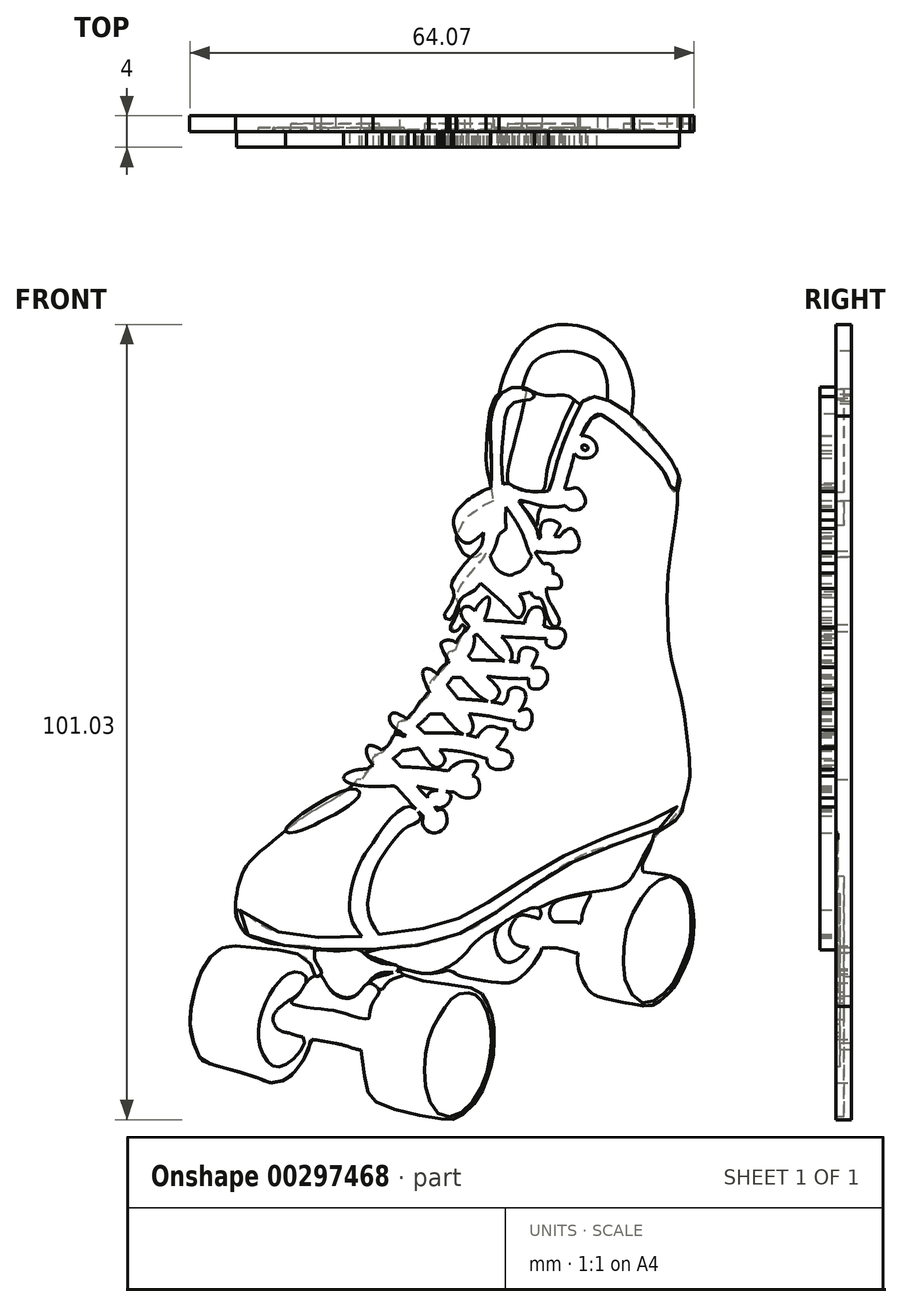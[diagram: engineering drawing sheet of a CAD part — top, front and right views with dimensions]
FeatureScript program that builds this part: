
annotation { "Feature Type Name" : "Feature", "Feature Type Description" : "" }
export const myFeature = defineFeature(function(context is Context, id is Id, definition is map)
    precondition{}
    {
        {
            var Q0;
            Q0=qCreatedBy(makeId("Front.planeOp"),FACE);
            var sketch = newSketch(context, id + "F0", { "sketchPlane" : qUnion([Q0])});
            skFitSpline(sketch, "E0", {"points": [v(-12.66, 16.22) * mm, v(-11.45, 15.9) * mm, v(-10.21, 15.64) * mm, v(-8.9, 15.37) * mm, v(-7.7, 15.13) * mm, v(-6.64, 14.98) * mm, v(-5.56, 15.1) * mm, v(-4.67, 15.72) * mm, v(-3.66, 16.57) * mm, v(-2.88, 17.5) * mm, v(-2.22, 18.59) * mm, v(-1.68, 19.8) * mm, v(-1.06, 21.19) * mm, v(-0.67, 22.58) * mm, v(-0.6, 23.51) * mm, v(-0.4, 25.03) * mm, v(-0.44, 26.3) * mm, v(-0.6, 27.55) * mm, v(-0.83, 28.64) * mm, v(-1.33, 30) * mm, v(-2.07, 30.88) * mm, v(-3.3, 31.47) * mm, v(-4.9, 31.78) * mm, v(-6.06, 31.97) * mm, v(-7.19, 32.17) * mm, v(-7.07, 32.9) * mm, v(-6.22, 34.57) * mm, v(-5.64, 36.04) * mm, v(-5.44, 36.86) * mm, v(-4.55, 37.44) * mm, v(-3.3, 38.18) * mm, v(-2.5, 38.8) * mm, v(-1.91, 39.61) * mm, v(-1.83, 40.62) * mm, v(-1.49, 41.24) * mm, v(-1.17, 42.64) * mm, v(-0.9, 44.35) * mm, v(-1.1, 47.49) * mm, v(-1.56, 51.33) * mm, v(-2.1, 54.51) * mm, v(-2.84, 57.19) * mm, v(-3.58, 60.72) * mm, v(-3.7, 63.04) * mm, v(-3.81, 67.66) * mm, v(-3.5, 71.7) * mm, v(-3.11, 74.18) * mm, v(-2.73, 76.66) * mm, v(-2.53, 79.03) * mm, v(-2.53, 80.07) * mm, v(-2.18, 81.24) * mm, v(-2.38, 82.79) * mm, v(-3.11, 83.92) * mm, v(-4.33, 85.57) * mm, v(-4.87, 86.43) * mm, v(-6.4, 87.78) * mm, v(-8.4, 89.91) * mm, v(-11.37, 91.78) * mm, v(-13.45, 92.22) * mm, v(-14.5, 91.87) * mm, v(-14.91, 91.44) * mm], "startDerivative": vector(80.46, -21.54) * mm, "endDerivative": vector(-30.96, -32.86) * mm});
            skFitSpline(sketch, "E1", {"points": [v(-14.91, 91.44) * mm, v(-16.65, 92.56) * mm, v(-18.46, 92.53) * mm, v(-20.26, 92.8) * mm, v(-21.34, 93.2) * mm, v(-23.4, 93.4) * mm, v(-25.2, 92.68) * mm, v(-25.7, 92.13) * mm, v(-26.31, 90.55) * mm, v(-26.58, 88.8) * mm, v(-26.74, 86.55) * mm, v(-26.78, 83.87) * mm, v(-26.5, 82.32) * mm, v(-26.2, 80.85) * mm, v(-25.92, 79.14) * mm], "startDerivative": vector(-22.92, 17.02) * mm, "endDerivative": vector(3.64, -24.68) * mm});
            skFitSpline(sketch, "E2", {"points": [v(-25.92, 79.14) * mm, v(-27.05, 78.6) * mm, v(-28.37, 77.7) * mm, v(-29.57, 76.73) * mm, v(-30.27, 75.41) * mm, v(-30.58, 74.37) * mm, v(-30.15, 73.32) * mm, v(-29.53, 72.39) * mm, v(-27.9, 71.77) * mm], "startDerivative": vector(-9.85, -4.24) * mm, "endDerivative": vector(11.11, -2.3) * mm});
            skFitSpline(sketch, "E3", {"points": [v(-28.83, 72.02) * mm, v(-28.34, 72.02) * mm, v(-27.85, 72.2) * mm, v(-27.2, 72.69) * mm, v(-27.05, 72.8) * mm, v(-26.89, 72.63) * mm, v(-26.92, 72.4) * mm, v(-27.27, 71.8) * mm, v(-27.89, 71.1) * mm, v(-28.43, 70.49) * mm, v(-29.17, 69.6) * mm, v(-29.71, 68.93) * mm, v(-30.15, 68.25) * mm, v(-30.5, 67.42) * mm, v(-30.62, 66.83) * mm, v(-30.36, 66.18) * mm, v(-30.31, 65.58) * mm, v(-30.53, 64.8) * mm, v(-30.93, 63.95) * mm, v(-31.36, 63.13) * mm, v(-31.2, 62.64) * mm, v(-30.68, 62.59) * mm, v(-30.37, 62.78) * mm, v(-30.08, 63.16) * mm, v(-29.81, 63.44) * mm, v(-29.54, 63.27) * mm, v(-29.5, 62.97) * mm, v(-29.62, 62.65) * mm, v(-29.94, 62.04) * mm, v(-30.25, 61.4) * mm, v(-30.47, 60.84) * mm, v(-30.65, 60.3) * mm, v(-31.49, 59.99) * mm, v(-31.86, 59.32) * mm, v(-31.84, 58.65) * mm, v(-32.17, 57.9) * mm, v(-33.63, 56.5) * mm, v(-34.14, 55.35) * mm, v(-34.1, 54.69) * mm, v(-35.05, 53.56) * mm, v(-35.98, 52.36) * mm, v(-37.1, 51.22) * mm, v(-37.91, 51.08) * mm, v(-38.38, 49.63) * mm, v(-40.18, 47.13) * mm, v(-41.12, 46.75) * mm, v(-41.24, 45.74) * mm, v(-42.4, 44.21) * mm, v(-42.56, 43.8) * mm, v(-43.08, 43.77) * mm, v(-44.07, 42.74) * mm, v(-49.8, 39.14) * mm, v(-54.36, 35.56) * mm, v(-57.32, 32.68) * mm, v(-58.52, 29) * mm, v(-58.33, 25.74) * mm, v(-55.92, 23.57) * mm, v(-52.02, 22.75) * mm, v(-48.7, 22.33) * mm, v(-48.59, 20.97) * mm, v(-47.75, 19.14) * mm, v(-48.48, 18.81) * mm, v(-49, 20.13) * mm, v(-50.97, 21.7) * mm, v(-55.18, 22.29) * mm, v(-59.17, 22.65) * mm, v(-60.7, 22.18) * mm, v(-62.47, 20.38) * mm, v(-63.78, 17.12) * mm, v(-64.4, 13.87) * mm, v(-64.22, 11.12) * mm, v(-63.24, 8.52) * mm, v(-62.47, 7.86) * mm, v(-55.44, 5.77) * mm, v(-55, 5.48) * mm, v(-53.6, 5.23) * mm, v(-51.7, 6.07) * mm, v(-50.42, 7.57) * mm, v(-49.43, 9.33) * mm, v(-49.07, 10.68) * mm, v(-48.74, 10.76) * mm, v(-42.84, 9.51) * mm, v(-42.62, 9.1) * mm, v(-42, 4.75) * mm, v(-40.31, 2.56) * mm, v(-32.22, 0.62) * mm, v(-30.5, 0.8) * mm, v(-28.01, 2.96) * mm, v(-26.58, 6.1) * mm, v(-26, 8.2) * mm, v(-25.78, 10.94) * mm, v(-26, 13.65) * mm, v(-26.99, 16) * mm, v(-28.49, 17.24) * mm, v(-36.87, 18.74) * mm, v(-37.71, 19.66) * mm, v(-34.13, 19.07) * mm, v(-31.53, 19.5) * mm, v(-30.43, 18.96) * mm, v(-25.56, 18) * mm, v(-22.63, 18.49) * mm, v(-19.8, 22.07) * mm, v(-19.63, 22.44) * mm, v(-15.27, 21.9) * mm, v(-15.2, 21.2) * mm, v(-14.9, 19.15) * mm, v(-13.66, 16.91) * mm, v(-12.66, 16.22) * mm], "startDerivative": vector(99.24, -6.04) * mm, "endDerivative": vector(125.3, -64.7) * mm});
            skFitSpline(sketch, "E4", {"points": [v(-25.2, 92.68) * mm, v(-20.46, 100.62) * mm, v(-11.73, 100) * mm, v(-8.4, 89.91) * mm], "startDerivative": vector(5.78, 27.5) * mm, "endDerivative": vector(-8.42, -35.04) * mm});
            skFitSpline(sketch, "E5", {"points": [v(-22.25, 93.4) * mm, v(-19.97, 97.43) * mm, v(-12.94, 97.22) * mm, v(-11.37, 91.78) * mm], "startDerivative": vector(4.24, 16.05) * mm, "endDerivative": vector(-0.4, -21.14) * mm});
            skSolve(sketch);
        }
        {
            var Q0;
            Q0=qCreatedBy(makeId("Front.planeOp"),FACE);
            var sketch = newSketch(context, id + "F1", { "sketchPlane" : qUnion([Q0])});
            skFitSpline(sketch, "E6", {"points": [v(-20.8, 94.94) * mm, v(-21.53, 93.88) * mm, v(-22.17, 90.77) * mm, v(-23.27, 86.35) * mm, v(-24.08, 81.7) * mm, v(-23.14, 80.94) * mm, v(-19.78, 80.34) * mm, v(-19.1, 82.9) * mm, v(-18, 86.43) * mm, v(-16.59, 90.05) * mm, v(-15.19, 93.62) * mm, v(-17.02, 94.56) * mm, v(-20.8, 94.94) * mm]});
            skFitSpline(sketch, "E7", {"points": [v(-22.28, 78.98) * mm, v(-19.9, 78.56) * mm, v(-20.09, 77.84) * mm, v(-20.39, 76.06) * mm, v(-21.32, 77.45) * mm, v(-22.28, 78.98) * mm]});
            skSolve(sketch);
        }
        {
            var Q0;
            Q0=qCreatedBy(makeId("Front.planeOp"),FACE);
            var sketch = newSketch(context, id + "F2", { "sketchPlane" : qUnion([Q0])});
            skFitSpline(sketch, "E8", {"points": [v(-22.6, 80.66) * mm, v(-19.23, 80.38) * mm, v(-16.76, 80.7) * mm, v(-15.8, 80.41) * mm, v(-15.58, 79.34) * mm, v(-16.8, 78.59) * mm, v(-19.44, 78.48) * mm, v(-22.6, 79.16) * mm, v(-22.09, 78.34) * mm, v(-21.12, 76.83) * mm, v(-20.37, 75.51) * mm, v(-20.2, 73.97) * mm, v(-20.55, 72.54) * mm, v(-21.02, 72.11) * mm, v(-21.55, 71.1) * mm, v(-22.27, 70.32) * mm, v(-23.27, 69.9) * mm, v(-23.92, 69.71) * mm, v(-25.45, 70.54) * mm, v(-26.31, 72.15) * mm, v(-27, 74.22) * mm, v(-27.14, 75.87) * mm, v(-26.67, 77.84) * mm, v(-25.96, 79.27) * mm, v(-24.52, 80.34) * mm, v(-23.63, 79.7) * mm, v(-23.13, 80.8) * mm, v(-22.6, 80.66) * mm]});
            skFitSpline(sketch, "E9", {"points": [v(-23.63, 79.7) * mm, v(-22.6, 79.16) * mm], "startDerivative": vector(1.04, -0.54) * mm, "endDerivative": vector(1.04, -0.54) * mm});
            skFitSpline(sketch, "E10", {"points": [v(-23.63, 79.7) * mm, v(-25.35, 76.3) * mm, v(-25.96, 74.9) * mm, v(-26.31, 72.15) * mm], "startDerivative": vector(-4.78, -9.57) * mm, "endDerivative": vector(-0.75, -8.95) * mm});
            skFitSpline(sketch, "E11", {"points": [v(-24.27, 78.41) * mm, v(-22.23, 75.12) * mm, v(-21.52, 73.04) * mm, v(-21.02, 72.11) * mm], "startDerivative": vector(5.39, -7.68) * mm, "endDerivative": vector(2.3, -3.63) * mm});
            skFitSpline(sketch, "E12", {"points": [v(-23.13, 80.8) * mm, v(-23.99, 81.38) * mm, v(-24.85, 81.17) * mm, v(-25.24, 80.8) * mm, v(-25.01, 80.25) * mm], "startDerivative": vector(-2.81, 2.66) * mm, "endDerivative": vector(1.71, -2.68) * mm});
            skFitSpline(sketch, "E13", {"points": [v(-25.24, 80.8) * mm, v(-26.31, 80.8) * mm, v(-30.07, 78.41) * mm, v(-30.9, 75.94) * mm, v(-29.43, 73.83) * mm, v(-27.15, 75.12) * mm], "startDerivative": vector(-6.78, 1.52) * mm, "endDerivative": vector(11.72, 10.78) * mm});
            skFitSpline(sketch, "E14", {"points": [v(-25.24, 80.8) * mm, v(-27.46, 79.16) * mm, v(-29.32, 76.94) * mm, v(-30.9, 75.94) * mm], "startDerivative": vector(-6.64, -4.1) * mm, "endDerivative": vector(-5.59, -2.73) * mm});
            skFitSpline(sketch, "E15", {"points": [v(-24.27, 78.41) * mm, v(-24.27, 75.62) * mm, v(-23.13, 72.11) * mm, v(-21.52, 73.04) * mm], "startDerivative": vector(-0.53, -7.18) * mm, "endDerivative": vector(6.33, 6.23) * mm});
            skFitSpline(sketch, "E16", {"points": [v(-24.27, 75.62) * mm, v(-25.14, 74.83) * mm, v(-25.63, 73.4) * mm, v(-26.31, 72.15) * mm], "startDerivative": vector(-3.21, -2.14) * mm, "endDerivative": vector(-2.25, -3.47) * mm});
            skFitSpline(sketch, "E17", {"points": [v(-25.63, 73.4) * mm, v(-23.87, 73.4) * mm], "startDerivative": vector(1.77, 0) * mm, "endDerivative": vector(1.77, 0) * mm});
            skFitSpline(sketch, "E18", {"points": [v(-27.15, 75.12) * mm, v(-27.46, 73.4) * mm, v(-29.25, 71.5) * mm, v(-30.9, 69.25) * mm, v(-31.22, 68.39) * mm, v(-30.9, 67.35) * mm, v(-31.54, 65.6) * mm, v(-32.15, 64.49) * mm, v(-31.4, 64.1) * mm, v(-30.29, 66.2) * mm, v(-29.6, 67.06) * mm, v(-27.94, 68.1) * mm, v(-26.31, 72.15) * mm], "startDerivative": vector(-0.42, -21.79) * mm, "endDerivative": vector(9.61, 37.07) * mm});
            skFitSpline(sketch, "E19", {"points": [v(-20.18, 74.4) * mm, v(-16.72, 74.4) * mm, v(-16.18, 73.4) * mm, v(-17.58, 72.61) * mm, v(-20.44, 72.74) * mm], "startDerivative": vector(12.88, 1.9) * mm, "endDerivative": vector(-10.29, 1.45) * mm});
            skFitSpline(sketch, "E20", {"points": [v(-20.55, 72.54) * mm, v(-19.66, 71.32) * mm, v(-18.94, 70.32) * mm, v(-19.15, 68.1) * mm, v(-18.69, 66.24) * mm, v(-17.5, 63.63) * mm, v(-18.37, 63.27) * mm, v(-19.87, 66.74) * mm, v(-20.55, 66.88) * mm, v(-22.27, 70) * mm], "startDerivative": vector(8.72, -13.24) * mm, "endDerivative": vector(-11.7, 29.04) * mm});
            skFitSpline(sketch, "E21", {"points": [v(-22.27, 70) * mm, v(-22.27, 70.32) * mm], "startDerivative": vector(0, 0.32) * mm, "endDerivative": vector(0, 0.32) * mm});
            skFitSpline(sketch, "E22", {"points": [v(-18.9, 70) * mm, v(-17.58, 69.64) * mm, v(-17.33, 68.28) * mm, v(-19.15, 68.1) * mm], "startDerivative": vector(4.73, -0.06) * mm, "endDerivative": vector(-6.4, 0.81) * mm});
            skFitSpline(sketch, "E23", {"points": [v(-27.5, 68.68) * mm, v(-23.99, 65.45) * mm, v(-22.6, 64.34) * mm, v(-21.98, 66.06) * mm, v(-26.73, 70.54) * mm], "startDerivative": vector(13.18, -11.25) * mm, "endDerivative": vector(-19.34, 12.92) * mm});
            skFitSpline(sketch, "E24", {"points": [v(-24.51, 69.06) * mm, v(-22.02, 69.4) * mm], "startDerivative": vector(2.5, 0.34) * mm, "endDerivative": vector(2.5, 0.34) * mm});
            skFitSpline(sketch, "E25", {"points": [v(-22.6, 67.26) * mm, v(-21.19, 67.59) * mm], "startDerivative": vector(1.4, 0.33) * mm, "endDerivative": vector(1.4, 0.33) * mm});
            skFitSpline(sketch, "E26", {"points": [v(-27, 68.1) * mm, v(-27.15, 66.38) * mm, v(-25.01, 66.49) * mm], "startDerivative": vector(-1.36, -4.53) * mm, "endDerivative": vector(5.2, 1.2) * mm});
            skFitSpline(sketch, "E27", {"points": [v(-30.04, 65.06) * mm, v(-29.28, 65.78) * mm, v(-28.35, 65.3) * mm, v(-27.15, 64.02) * mm, v(-23.63, 60.2) * mm, v(-23.99, 58.72) * mm, v(-27.53, 61.77) * mm, v(-30.04, 65.06) * mm]});
            skFitSpline(sketch, "E28", {"points": [v(-27.15, 64.02) * mm, v(-20.2, 63.41) * mm, v(-18.37, 62.7) * mm, v(-18, 61.84) * mm, v(-19.15, 61.66) * mm, v(-24.86, 61.93) * mm], "startDerivative": vector(25.61, -1.63) * mm, "endDerivative": vector(-23.17, 1.13) * mm});
            skFitSpline(sketch, "E29", {"points": [v(-28.97, 63.27) * mm, v(-29.5, 61.95) * mm, v(-27.94, 62.2) * mm], "startDerivative": vector(-2.08, -3.5) * mm, "endDerivative": vector(4.1, 1.3) * mm});
            skFitSpline(sketch, "E30", {"points": [v(-32.54, 60.76) * mm, v(-32.15, 61.37) * mm, v(-30.9, 61.3) * mm, v(-27.53, 57.69) * mm, v(-25.14, 55) * mm, v(-25.63, 53.93) * mm, v(-27, 53.9) * mm, v(-32.54, 60.76) * mm]});
            skFitSpline(sketch, "E31", {"points": [v(-28.62, 58.94) * mm, v(-21.02, 58.08) * mm, v(-20.55, 57.04) * mm, v(-22.27, 56.58) * mm, v(-26.73, 56.9) * mm], "startDerivative": vector(25.3, -0.12) * mm, "endDerivative": vector(-16.35, 1.8) * mm});
            skFitSpline(sketch, "E32", {"points": [v(-32.3, 56.8) * mm, v(-29.92, 56.73) * mm], "startDerivative": vector(2.37, -0.06) * mm, "endDerivative": vector(2.37, -0.06) * mm});
            skFitSpline(sketch, "E33", {"points": [v(-32.3, 56.8) * mm, v(-31.54, 58.86) * mm], "startDerivative": vector(0.76, 2.07) * mm, "endDerivative": vector(0.76, 2.07) * mm});
            skFitSpline(sketch, "E34", {"points": [v(-34.87, 57.26) * mm, v(-29.71, 49.53) * mm, v(-28.5, 50.46) * mm, v(-30.9, 54.72) * mm, v(-33.22, 57.33) * mm, v(-34.33, 57.87) * mm, v(-34.87, 57.26) * mm]});
            skFitSpline(sketch, "E35", {"points": [v(-36.12, 52.1) * mm, v(-34.72, 54.07) * mm, v(-33.57, 54.09) * mm], "startDerivative": vector(2.22, 4.3) * mm, "endDerivative": vector(2.92, -0.62) * mm});
            skFitSpline(sketch, "E36", {"points": [v(-36.12, 52.1) * mm, v(-32.3, 52.1) * mm], "startDerivative": vector(3.83, 0) * mm, "endDerivative": vector(3.83, 0) * mm});
            skFitSpline(sketch, "E37", {"points": [v(-30.35, 54.04) * mm, v(-24.51, 53.32) * mm, v(-22.27, 52.1) * mm, v(-22.27, 51.28) * mm, v(-25.63, 51.67) * mm, v(-29.01, 52.1) * mm], "startDerivative": vector(22.58, -1.55) * mm, "endDerivative": vector(-14.49, 1.13) * mm});
            skFitSpline(sketch, "E38", {"points": [v(-37.98, 52.1) * mm, v(-38.88, 52.1) * mm, v(-38.91, 50.89) * mm, v(-35.83, 48.3) * mm, v(-33.26, 45.34) * mm, v(-32.04, 46.2) * mm, v(-33.44, 48.27) * mm, v(-35.3, 50.31) * mm, v(-37.98, 52.1) * mm]});
            skFitSpline(sketch, "E39", {"points": [v(-34.66, 49.67) * mm, v(-29.71, 49.53) * mm, v(-26.31, 48.45) * mm, v(-25.01, 47.3) * mm, v(-25.24, 46.34) * mm, v(-29, 47.1) * mm, v(-32.73, 47.53) * mm], "startDerivative": vector(23.75, 0.74) * mm, "endDerivative": vector(-18.49, 0.53) * mm});
            skFitSpline(sketch, "E40", {"points": [v(-35.38, 47.77) * mm, v(-39.1, 47.63) * mm, v(-38.3, 48.95) * mm, v(-36.98, 49.28) * mm], "startDerivative": vector(-11.7, -2.16) * mm, "endDerivative": vector(4.88, 0.06) * mm});
            skFitSpline(sketch, "E41", {"points": [v(-41.7, 48.06) * mm, v(-41.85, 46.66) * mm, v(-39.52, 44.05) * mm, v(-37.48, 41.97) * mm, v(-35.23, 39.54) * mm, v(-33.4, 38.43) * mm, v(-33, 39.5) * mm, v(-34.44, 41.69) * mm, v(-36.73, 44.2) * mm, v(-38.7, 46.48) * mm, v(-41.7, 48.06) * mm]});
            skFitSpline(sketch, "E42", {"points": [v(-37.68, 45.41) * mm, v(-32.97, 45.05) * mm, v(-29.43, 43.9) * mm, v(-29.43, 42.51) * mm, v(-35.6, 42.93) * mm], "startDerivative": vector(16.62, -0.81) * mm, "endDerivative": vector(-25.08, 5.27) * mm});
            skFitSpline(sketch, "E43", {"points": [v(-40.68, 45.11) * mm, v(-44.07, 44.77) * mm, v(-44.92, 43.9) * mm, v(-42.92, 43.01) * mm, v(-38.41, 42.98) * mm], "startDerivative": vector(-13.34, 0.06) * mm, "endDerivative": vector(14.3, 0.9) * mm});
            skFitSpline(sketch, "E44", {"points": [v(-34.8, 39.15) * mm, v(-34.74, 37.75) * mm, v(-33.26, 36.98) * mm, v(-31.8, 38.3) * mm, v(-32.3, 39.92) * mm, v(-32.91, 39.88) * mm, v(-33.1, 39.87) * mm], "startDerivative": vector(-1.43, -8) * mm, "endDerivative": vector(-2.39, 0.23) * mm});
            skFitSpline(sketch, "E45", {"points": [v(-30.9, 42.18) * mm, v(-29.71, 41.5) * mm, v(-27.94, 41.88) * mm, v(-27.94, 43.9) * mm, v(-29.71, 44.17) * mm], "startDerivative": vector(4.6, -3.74) * mm, "endDerivative": vector(-8.3, -0.98) * mm});
            skFitSpline(sketch, "E46", {"points": [v(-26.73, 46.43) * mm, v(-26.31, 45.34) * mm, v(-23.99, 45.34) * mm, v(-23.63, 46.94) * mm, v(-25.24, 47.69) * mm], "startDerivative": vector(0.36, -5.98) * mm, "endDerivative": vector(-7.87, 1.6) * mm});
            skFitSpline(sketch, "E47", {"points": [v(-23.13, 51.18) * mm, v(-23.13, 50.52) * mm, v(-21.68, 50.14) * mm, v(-21.02, 51.2) * mm, v(-21.02, 52.1) * mm, v(-21.52, 52.73) * mm, v(-22.6, 52.46) * mm], "startDerivative": vector(-1.73, -5.12) * mm, "endDerivative": vector(-6.77, -3.16) * mm});
            skFitSpline(sketch, "E48", {"points": [v(-21.42, 56.64) * mm, v(-21.16, 55.41) * mm, v(-19.76, 55.46) * mm, v(-19, 56.82) * mm, v(-19.59, 57.93) * mm, v(-20.82, 57.92) * mm], "startDerivative": vector(-0.2, -7.64) * mm, "endDerivative": vector(-6.91, -1.34) * mm});
            skFitSpline(sketch, "E49", {"points": [v(-19.15, 61.66) * mm, v(-19.15, 61) * mm, v(-17.89, 60.48) * mm, v(-16.78, 61.66) * mm, v(-17.08, 62.82) * mm, v(-18.8, 63.02) * mm], "startDerivative": vector(-1.36, -4.7) * mm, "endDerivative": vector(-8.73, -0.55) * mm});
            skFitSpline(sketch, "E50", {"points": [v(-18.38, 68) * mm, v(-18.38, 66.74) * mm, v(-16.23, 67.37) * mm, v(-15.84, 68.74) * mm, v(-16.6, 69.84) * mm, v(-17.58, 69.64) * mm], "startDerivative": vector(-2.37, -8.57) * mm, "endDerivative": vector(-6.05, -2.83) * mm});
            skFitSpline(sketch, "E51", {"points": [v(-17.5, 74.6) * mm, v(-16.1, 75.67) * mm, v(-15.25, 74.87) * mm, v(-15.03, 73.42) * mm, v(-15.71, 72.74) * mm, v(-17.06, 72.74) * mm], "startDerivative": vector(6.4, 7.02) * mm, "endDerivative": vector(-7.17, 0.87) * mm});
            skFitSpline(sketch, "E52", {"points": [v(-16.21, 80.66) * mm, v(-15.29, 80.82) * mm, v(-14.44, 79.97) * mm, v(-14.35, 78.57) * mm, v(-15.84, 77.97) * mm, v(-16.8, 78.59) * mm], "startDerivative": vector(5.45, 2.1) * mm, "endDerivative": vector(-4.2, 4.39) * mm});
            skFitSpline(sketch, "E53", {"points": [v(-14.74, 87.42) * mm, v(-13.25, 86.91) * mm, v(-12.73, 85.68) * mm, v(-13.54, 84.7) * mm, v(-15.37, 84.95) * mm, v(-15.67, 86.23) * mm, v(-14.74, 87.42) * mm]});
            skFitSpline(sketch, "E54", {"points": [v(-14.35, 86.27) * mm, v(-14.65, 86.1) * mm, v(-14.3, 85.6) * mm, v(-13.84, 85.85) * mm, v(-14.35, 86.27) * mm]});
            skSolve(sketch);
        }
        {
            var Q0;
            Q0=qCreatedBy(makeId("Front.planeOp"),FACE);
            var sketch = newSketch(context, id + "F3", { "sketchPlane" : qUnion([Q0])});
            skFitSpline(sketch, "E55", {"points": [v(-58.39, 27.16) * mm, v(-57.8, 24.72) * mm, v(-55.92, 23.57) * mm, v(-52.14, 22.64) * mm, v(-47.85, 22.21) * mm, v(-42.03, 22.21) * mm, v(-36.93, 22.55) * mm, v(-34.42, 22.9) * mm, v(-29.2, 24.6) * mm, v(-25.71, 26.76) * mm, v(-21.8, 29.52) * mm, v(-18.1, 32.07) * mm, v(-13.27, 34.4) * mm, v(-9.32, 35.85) * mm, v(-3.8, 38.1) * mm, v(-2.3, 40.01) * mm, v(-2.69, 40.3) * mm, v(-4.26, 39.42) * mm, v(-8.42, 37.55) * mm, v(-12.88, 35.93) * mm, v(-17.43, 33.77) * mm, v(-22.32, 30.92) * mm, v(-25.67, 28.71) * mm, v(-28.26, 27.27) * mm, v(-30.52, 26.04) * mm, v(-33.57, 25.14) * mm, v(-36.93, 24.5) * mm, v(-42.88, 23.83) * mm, v(-47.42, 23.66) * mm, v(-51.38, 24.12) * mm, v(-55.24, 25.19) * mm, v(-58.39, 27.16) * mm]});
            skFitSpline(sketch, "E56", {"points": [v(-42.58, 23.85) * mm, v(-43.9, 25.95) * mm, v(-44.03, 29.35) * mm, v(-42.88, 33.09) * mm, v(-41.18, 35.76) * mm, v(-36.63, 40.35) * mm, v(-35.1, 38.87) * mm, v(-36.68, 37.8) * mm, v(-38.04, 36.66) * mm, v(-39.86, 34.28) * mm, v(-41.18, 31.64) * mm, v(-41.69, 29.3) * mm, v(-41.77, 26.8) * mm, v(-40.4, 24.07) * mm], "startDerivative": vector(-22.05, 27.05) * mm, "endDerivative": vector(22.25, -34.4) * mm});
            skFitSpline(sketch, "E57", {"points": [v(-34.14, 41.95) * mm, v(-31.36, 41.85) * mm, v(-32.83, 40.18) * mm, v(-34.14, 41.95) * mm]});
            skFitSpline(sketch, "E58", {"points": [v(-31.97, 44.18) * mm, v(-30.3, 45.9) * mm, v(-27.98, 45.8) * mm, v(-28.33, 44.53) * mm, v(-29.54, 43.52) * mm, v(-30.9, 43.82) * mm, v(-31.97, 44.18) * mm]});
            skFitSpline(sketch, "E59", {"points": [v(-26.66, 50.44) * mm, v(-28.23, 48.32) * mm, v(-27.17, 47.86) * mm, v(-26.06, 47.46) * mm, v(-24.14, 49.94) * mm, v(-25, 50.24) * mm, v(-26.66, 50.44) * mm]});
            skFitSpline(sketch, "E60", {"points": [v(-23.78, 55.24) * mm, v(-24.24, 53.83) * mm, v(-25.35, 52.56) * mm, v(-23.38, 51.96) * mm, v(-21.91, 54.94) * mm, v(-23.78, 55.24) * mm]});
            skFitSpline(sketch, "E61", {"points": [v(-22.32, 60.34) * mm, v(-22.82, 58.47) * mm, v(-23.38, 57.31) * mm, v(-21.26, 56.9) * mm, v(-20.95, 58.22) * mm, v(-20.35, 60.04) * mm, v(-22.32, 60.34) * mm]});
            skFitSpline(sketch, "E62", {"points": [v(-20.95, 65.55) * mm, v(-21.76, 62.67) * mm, v(-20.25, 62.11) * mm, v(-19.49, 65.1) * mm, v(-20.95, 65.55) * mm]});
            skFitSpline(sketch, "E63", {"points": [v(-19.7, 70.95) * mm, v(-18.93, 69.44) * mm, v(-18.38, 70.85) * mm, v(-19.7, 70.95) * mm]});
            skFitSpline(sketch, "E64", {"points": [v(-19.49, 76.56) * mm, v(-19.9, 74.09) * mm, v(-19.59, 72.92) * mm, v(-18.38, 72.77) * mm, v(-18.12, 74.6) * mm, v(-17.47, 76.16) * mm, v(-19.49, 76.56) * mm]});
            skFitSpline(sketch, "E65", {"points": [v(-14.18, 92.12) * mm, v(-15.65, 89.6) * mm, v(-16.76, 87.12) * mm, v(-17.97, 83.48) * mm, v(-18.63, 81.06) * mm, v(-19.08, 78.58) * mm, v(-17.22, 78.68) * mm, v(-16.96, 79.85) * mm, v(-16.2, 82.83) * mm, v(-15.1, 86.62) * mm, v(-12.92, 90.1) * mm, v(-11.66, 89.85) * mm, v(-8.17, 86.97) * mm, v(-5.65, 84.5) * mm, v(-3.83, 82.17) * mm, v(-2.97, 80.35) * mm, v(-2.26, 81.77) * mm, v(-3.98, 85.25) * mm, v(-7.82, 89.6) * mm, v(-11.91, 92.17) * mm, v(-14.18, 92.12) * mm]});
            skFitSpline(sketch, "E66", {"points": [v(-20.85, 92.98) * mm, v(-23.63, 93.54) * mm, v(-25.8, 91.26) * mm, v(-26.26, 87.78) * mm, v(-26.16, 82.52) * mm, v(-25.8, 79.04) * mm, v(-24.64, 78.99) * mm, v(-24.7, 81.41) * mm, v(-24.8, 85.7) * mm, v(-24.54, 88.74) * mm, v(-23.83, 91.21) * mm, v(-21.91, 91.97) * mm, v(-20.75, 92.27) * mm, v(-20.85, 92.98) * mm]});
            skFitSpline(sketch, "E67", {"points": [v(-28.06, 65.6) * mm, v(-28.16, 64.65) * mm, v(-27.35, 63.8) * mm, v(-26.4, 66.52) * mm, v(-26.64, 66.97) * mm, v(-28.06, 65.6) * mm]});
            skFitSpline(sketch, "E68", {"points": [v(-29.17, 62.73) * mm, v(-30.74, 60.36) * mm, v(-29.42, 59.3) * mm, v(-28.31, 61.77) * mm, v(-29.17, 62.73) * mm]});
            skFitSpline(sketch, "E69", {"points": [v(-31.65, 58.54) * mm, v(-32.96, 57.12) * mm, v(-32.5, 56.31) * mm, v(-32.05, 55.7) * mm, v(-30.89, 57.53) * mm, v(-31.65, 58.54) * mm]});
            skFitSpline(sketch, "E70", {"points": [v(-34.12, 54.8) * mm, v(-35.33, 53.08) * mm, v(-36.75, 51.46) * mm, v(-36, 50.55) * mm, v(-35.33, 50.76) * mm, v(-33.21, 53.64) * mm, v(-34.12, 54.8) * mm]});
            skFitSpline(sketch, "E71", {"points": [v(-38.31, 49.5) * mm, v(-39.27, 48.13) * mm, v(-40.03, 47.42) * mm, v(-39.07, 46.51) * mm, v(-38.47, 46.56) * mm, v(-36.95, 48.58) * mm, v(-38.31, 49.5) * mm]});
            skFitSpline(sketch, "E72", {"points": [v(-41.3, 45.55) * mm, v(-42.15, 44.04) * mm, v(-40.54, 44.24) * mm, v(-40.13, 44.74) * mm, v(-41.3, 45.55) * mm]});
            skFitSpline(sketch, "E73", {"points": [v(-44.12, 42.57) * mm, v(-52.3, 37.32) * mm, v(-50.7, 37.16) * mm, v(-47.96, 38.38) * mm, v(-45.64, 39.54) * mm, v(-42.88, 41.91) * mm, v(-44.12, 42.57) * mm]});
            skSolve(sketch);
        }
        {
            var Q0;
            Q0=qCreatedBy(makeId("Front.planeOp"),FACE);
            var sketch = newSketch(context, id + "F4", { "sketchPlane" : qUnion([Q0])});
            skFitSpline(sketch, "E74", {"points": [v(-42.54, 21.64) * mm, v(-38.35, 20.14) * mm, v(-34.06, 19.15) * mm, v(-29.97, 21.14) * mm, v(-27.18, 23.93) * mm, v(-21.3, 26.93) * mm, v(-21.2, 26.93) * mm], "startDerivative": vector(22.2, -7.62) * mm, "endDerivative": vector(1.93, -0.77) * mm});
            skFitSpline(sketch, "E75", {"points": [v(-21.2, 26.93) * mm, v(-16.3, 28.92) * mm, v(-10.72, 29.92) * mm, v(-8.53, 31.01) * mm, v(-6.73, 34.2) * mm, v(-5.44, 37.1) * mm, v(-9.83, 35.8) * mm, v(-13.52, 34.6) * mm, v(-17.5, 32.51) * mm, v(-20.4, 30.42) * mm, v(-23.79, 28.22) * mm, v(-27.38, 25.83) * mm, v(-30.77, 24.03) * mm, v(-34.26, 23.04) * mm, v(-39.45, 22.44) * mm, v(-42.54, 21.64) * mm], "startDerivative": vector(60.2, 29.93) * mm, "endDerivative": vector(-47.31, -15.12) * mm});
            skSolve(sketch);
        }
        {
            var Q0;
            Q0=qCreatedBy(makeId("Front.planeOp"),FACE);
            var sketch = newSketch(context, id + "F5", { "sketchPlane" : qUnion([Q0])});
            skFitSpline(sketch, "E76", {"points": [v(-48.6, 21.94) * mm, v(-47.96, 19.34) * mm, v(-46.34, 16.87) * mm, v(-44.08, 16.1) * mm, v(-42.04, 17.71) * mm, v(-40.14, 19.2) * mm, v(-38.16, 19.4) * mm, v(-38.02, 20.04) * mm, v(-40.14, 20.46) * mm, v(-42.32, 21.66) * mm, v(-43.1, 22.16) * mm, v(-46.06, 22.02) * mm, v(-48.6, 21.94) * mm]});
            skSolve(sketch);
        }
        {
            var Q0;
            Q0=qCreatedBy(makeId("Front.planeOp"),FACE);
            var sketch = newSketch(context, id + "F6", { "sketchPlane" : qUnion([Q0])});
            skFitSpline(sketch, "E77", {"points": [v(-49.61, 18.53) * mm, v(-51.1, 19.36) * mm, v(-52.87, 18.36) * mm, v(-54.3, 16.46) * mm, v(-55.66, 12.66) * mm, v(-55.37, 9.4) * mm, v(-53.82, 7.39) * mm, v(-51.51, 8.1) * mm, v(-49.97, 10.94) * mm, v(-53.11, 11.95) * mm, v(-53.59, 13.9) * mm, v(-51.87, 15.69) * mm, v(-50.68, 16.52) * mm, v(-49.61, 18.53) * mm]});
            skFitSpline(sketch, "E78", {"points": [v(-25.6, 24.29) * mm, v(-25.48, 21.97) * mm, v(-24.23, 20.55) * mm, v(-22.4, 21.26) * mm, v(-21.39, 22.86) * mm, v(-23.28, 23.28) * mm, v(-23.82, 24.7) * mm, v(-23.16, 25.95) * mm, v(-22.51, 26.24) * mm, v(-20.2, 26) * mm, v(-20.08, 27.37) * mm, v(-22.8, 26.66) * mm, v(-24.7, 25.47) * mm, v(-25.6, 24.29) * mm]});
            skSolve(sketch);
        }
        {
            var Q0;
            Q0 = qSketchRegion(id + "F0", true);
            extrude(context, id + "F7", {"entities" : qUnion([Q0]), "oppositeDirection" : true, "depth" : 2 * mm});
        }
        {
            var Q0;
            Q0 = qSketchRegion(id + "F1", true);
            extrude(context, id + "F8", {"entities" : qUnion([Q0]), "operationType" : NewBodyOperationType.REMOVE, "oppositeDirection" : true, "depth" : 1 * mm});
        }
        {
            var Q0;
            Q0 = qSketchRegion(id + "F2", true);
            extrude(context, id + "F9", {"entities" : qUnion([Q0]), "operationType" : NewBodyOperationType.ADD, "depth" : 2 * mm});
        }
        {
            var Q0;
            Q0 = qSketchRegion(id + "F3", true);
            extrude(context, id + "F10", {"entities" : qUnion([Q0]), "operationType" : NewBodyOperationType.ADD, "depth" : 2 * mm});
        }
        {
            var Q0;
            Q0 = qSketchRegion(id + "F4", true);
            extrude(context, id + "F11", {"entities" : qUnion([Q0]), "operationType" : NewBodyOperationType.REMOVE, "oppositeDirection" : true, "depth" : 0.25 * mm});
        }
        {
            var Q0;
            Q0 = qSketchRegion(id + "F5", true);
            extrude(context, id + "F12", {"entities" : qUnion([Q0]), "operationType" : NewBodyOperationType.REMOVE, "oppositeDirection" : true, "depth" : 0.5 * mm});
        }
        {
            var Q0;
            Q0 = qSketchRegion(id + "F6", true);
            extrude(context, id + "F13", {"entities" : qUnion([Q0]), "operationType" : NewBodyOperationType.REMOVE, "oppositeDirection" : true, "depth" : 0.5 * mm});
        }
        {
            var Q0;
            Q0=qCreatedBy(makeId("Front.planeOp"),FACE);
            var sketch = newSketch(context, id + "F14", { "sketchPlane" : qUnion([Q0])});
            skFitSpline(sketch, "E79", {"points": [v(-41.44, 18.03) * mm, v(-40.34, 18.76) * mm, v(-39.02, 19.12) * mm, v(-37.85, 19.42) * mm, v(-37.12, 19.05) * mm, v(-38.22, 18.61) * mm, v(-39.6, 17.66) * mm, v(-40.2, 17.08) * mm, v(-41.44, 18.03) * mm]});
            skFitSpline(sketch, "E80", {"points": [v(-18.19, 28.05) * mm, v(-18.43, 25.9) * mm, v(-15.05, 25.35) * mm, v(-14.62, 26.4) * mm, v(-14.07, 28.05) * mm, v(-13.58, 29.22) * mm, v(-15.24, 28.97) * mm, v(-18.19, 28.05) * mm]});
            skSolve(sketch);
        }
        {
            var Q0;
            Q0 = qSketchRegion(id + "F14", true);
            extrude(context, id + "F15", {"entities" : qUnion([Q0]), "operationType" : NewBodyOperationType.REMOVE, "oppositeDirection" : true, "depth" : 0.5 * mm});
        }
        {
            var Q0;
            Q0=qCreatedBy(makeId("Front.planeOp"),FACE);
            var sketch = newSketch(context, id + "F16", { "sketchPlane" : qUnion([Q0])});
            skFitSpline(sketch, "E81", {"points": [v(-52.17, 15.36) * mm, v(-49.56, 15) * mm, v(-45.4, 14.14) * mm, v(-42, 13.36) * mm, v(-42.26, 11.62) * mm, v(-42.44, 9.53) * mm, v(-44.43, 9.88) * mm, v(-46.17, 10.32) * mm, v(-48.34, 10.84) * mm, v(-50.26, 11.1) * mm, v(-52.86, 12.05) * mm, v(-53.9, 13.36) * mm, v(-52.17, 15.36) * mm]});
            skFitSpline(sketch, "E82", {"points": [v(-15, 25.46) * mm, v(-17.2, 25.67) * mm, v(-20.19, 26.11) * mm, v(-22.6, 26.48) * mm, v(-23.48, 25.24) * mm, v(-23.62, 23.7) * mm, v(-22.9, 22.75) * mm, v(-20.26, 22.39) * mm, v(-17.2, 22.24) * mm, v(-15.07, 21.8) * mm, v(-15.36, 23.4) * mm, v(-15, 25.46) * mm]});
            skSolve(sketch);
        }
        {
            var Q0;
            Q0 = qSketchRegion(id + "F16", true);
            extrude(context, id + "F17", {"entities" : qUnion([Q0]), "operationType" : NewBodyOperationType.ADD, "oppositeDirection" : true, "depth" : 2 * mm});
        }
        {
            var Q0;
            Q0=qCreatedBy(makeId("Front.planeOp"),FACE);
            var sketch = newSketch(context, id + "F18", { "sketchPlane" : qUnion([Q0])});
            skFitSpline(sketch, "E83", {"points": [v(-49.54, 18.11) * mm, v(-47.94, 18.9) * mm, v(-46.77, 17.25) * mm, v(-44.93, 16.02) * mm, v(-43.2, 16.45) * mm, v(-41.67, 17.86) * mm, v(-40.38, 16.88) * mm, v(-40.93, 15.9) * mm, v(-41.61, 14.12) * mm, v(-41.73, 13.38) * mm, v(-44.2, 13.87) * mm, v(-46.59, 14.48) * mm, v(-49.72, 14.85) * mm, v(-51.57, 15.47) * mm, v(-50.77, 16.33) * mm, v(-49.54, 18.11) * mm]});
            skSolve(sketch);
        }
        {
            var Q0;
            Q0 = qSketchRegion(id + "F18", true);
            extrude(context, id + "F19", {"entities" : qUnion([Q0]), "operationType" : NewBodyOperationType.REMOVE, "oppositeDirection" : true, "depth" : 1 * mm});
        }
        {
            var Q0;
            Q0=qCreatedBy(makeId("Front.planeOp"),FACE);
            var sketch = newSketch(context, id + "F20", { "sketchPlane" : qUnion([Q0])});
            skFitSpline(sketch, "E84", {"points": [v(-29.06, 16.69) * mm, v(-30.74, 16.32) * mm, v(-31.99, 14.85) * mm, v(-33.35, 12.7) * mm, v(-34.42, 9.38) * mm, v(-34.42, 4.33) * mm, v(-32.43, 1.08) * mm, v(-29.55, 1.78) * mm, v(-26.93, 5.91) * mm, v(-26.15, 10.71) * mm, v(-26.86, 14.74) * mm, v(-28, 16.29) * mm, v(-29.06, 16.69) * mm]});
            skFitSpline(sketch, "E85", {"points": [v(-3.48, 31.43) * mm, v(-5.13, 30.84) * mm, v(-6.74, 29.16) * mm, v(-8.7, 25.6) * mm, v(-9.35, 21.37) * mm, v(-8.95, 17.7) * mm, v(-7, 15.38) * mm, v(-5.16, 15.9) * mm, v(-3.33, 17.55) * mm, v(-1.96, 20.16) * mm, v(-1.03, 22.64) * mm, v(-0.78, 25.31) * mm, v(-0.94, 27.86) * mm, v(-1.37, 29.22) * mm, v(-2, 30.5) * mm, v(-2.74, 31.09) * mm, v(-3.48, 31.43) * mm]});
            skSolve(sketch);
        }
        {
            var Q0;
            Q0 = qSketchRegion(id + "F20", true);
            extrude(context, id + "F21", {"entities" : qUnion([Q0]), "operationType" : NewBodyOperationType.REMOVE, "oppositeDirection" : true, "depth" : 1 * mm});
        }
    });
